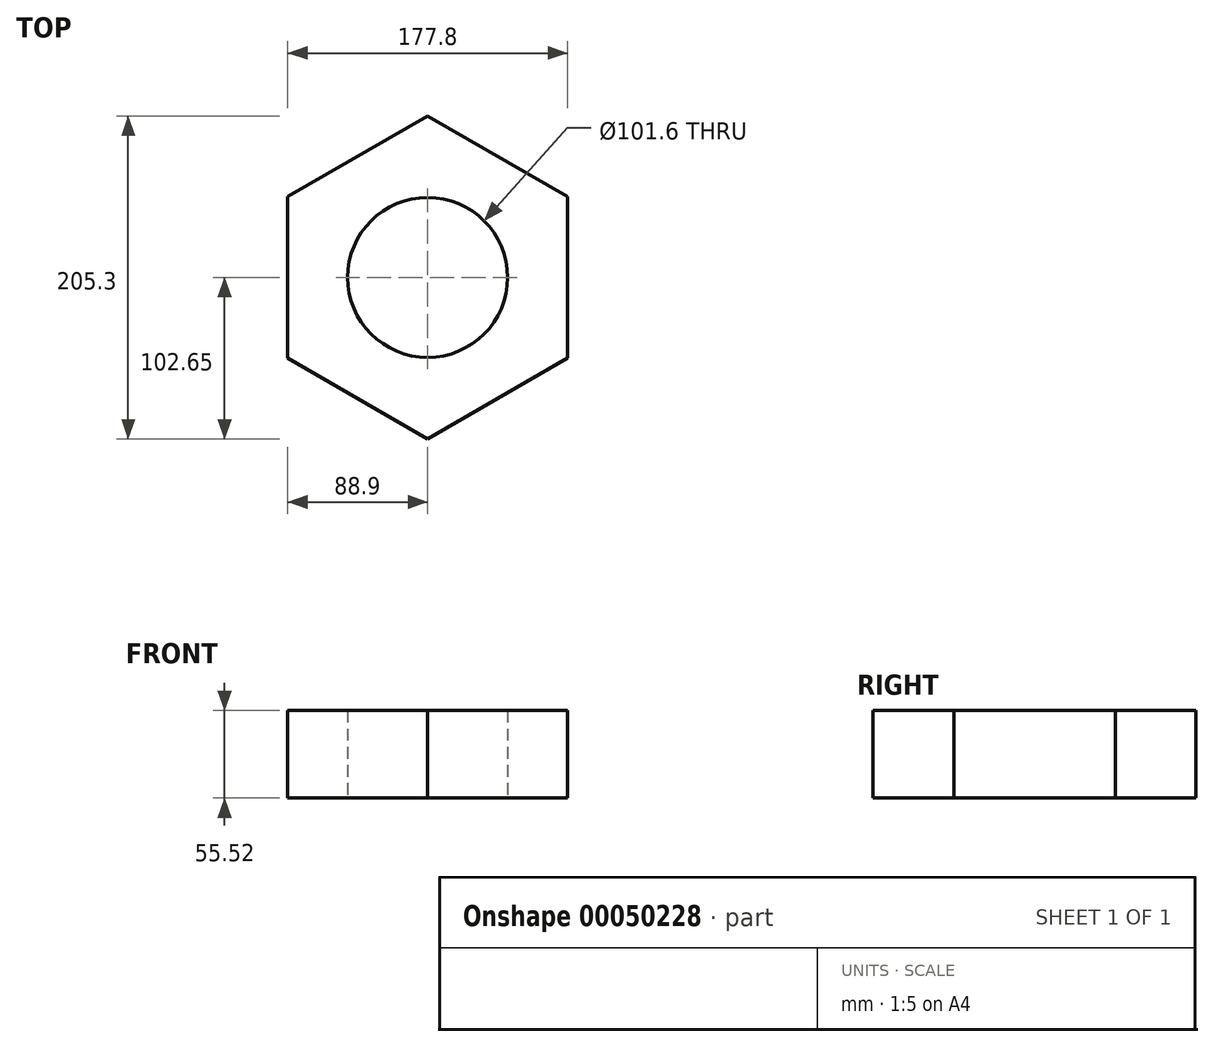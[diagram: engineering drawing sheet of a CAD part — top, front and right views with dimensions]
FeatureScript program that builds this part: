
annotation { "Feature Type Name" : "Feature", "Feature Type Description" : "" }
export const myFeature = defineFeature(function(context is Context, id is Id, definition is map)
    precondition{}
    {
        {
            var Q0;
            Q0=qCreatedBy(makeId("Top.planeOp"),FACE);
            var sketch = newSketch(context, id + "F0", { "sketchPlane" : qUnion([Q0])});
            skCircle(sketch, "E0.cCircle", {"center": v(0, 0) * mm, "radius": 88.9 * mm, "construction": true});
            skLineSegment(sketch, "E0.0", {"start": v(0, 102.65) * mm, "end": v(88.9, 51.33) * mm});
            skLineSegment(sketch, "E0.1", {"start": v(88.9, 51.33) * mm, "end": v(88.9, -51.33) * mm});
            skLineSegment(sketch, "E0.2", {"start": v(88.9, -51.33) * mm, "end": v(0, -102.65) * mm});
            skLineSegment(sketch, "E0.3", {"start": v(0, -102.65) * mm, "end": v(-88.9, -51.33) * mm});
            skLineSegment(sketch, "E0.4", {"start": v(-88.9, -51.33) * mm, "end": v(-88.9, 51.33) * mm});
            skLineSegment(sketch, "E0.5", {"start": v(-88.9, 51.33) * mm, "end": v(0, 102.65) * mm});
            skPoint(sketch, "E0.0.midPoint", {"position": v(44.45, 76.99) * mm});
            skCircle(sketch, "E1", {"center": v(0, 0) * mm, "radius": 50.8 * mm});
            skSolve(sketch);
        }
        {
            var Q0;
            Q0=makeQuery(id+"F0.imprint","IMPRINT",FACE,{"disambiguationData":[TD([[makeQuery(id+"F0.imprint","IMPRINT",EDGE,{"derivedFrom":sQuery(id+"F0.wireOp",EDGE,"E0.0")}),-1.0]])]});
            extrude(context, id + "F1", {"entities" : qUnion([Q0]), "depth" : 55.52 * mm});
        }
    });
